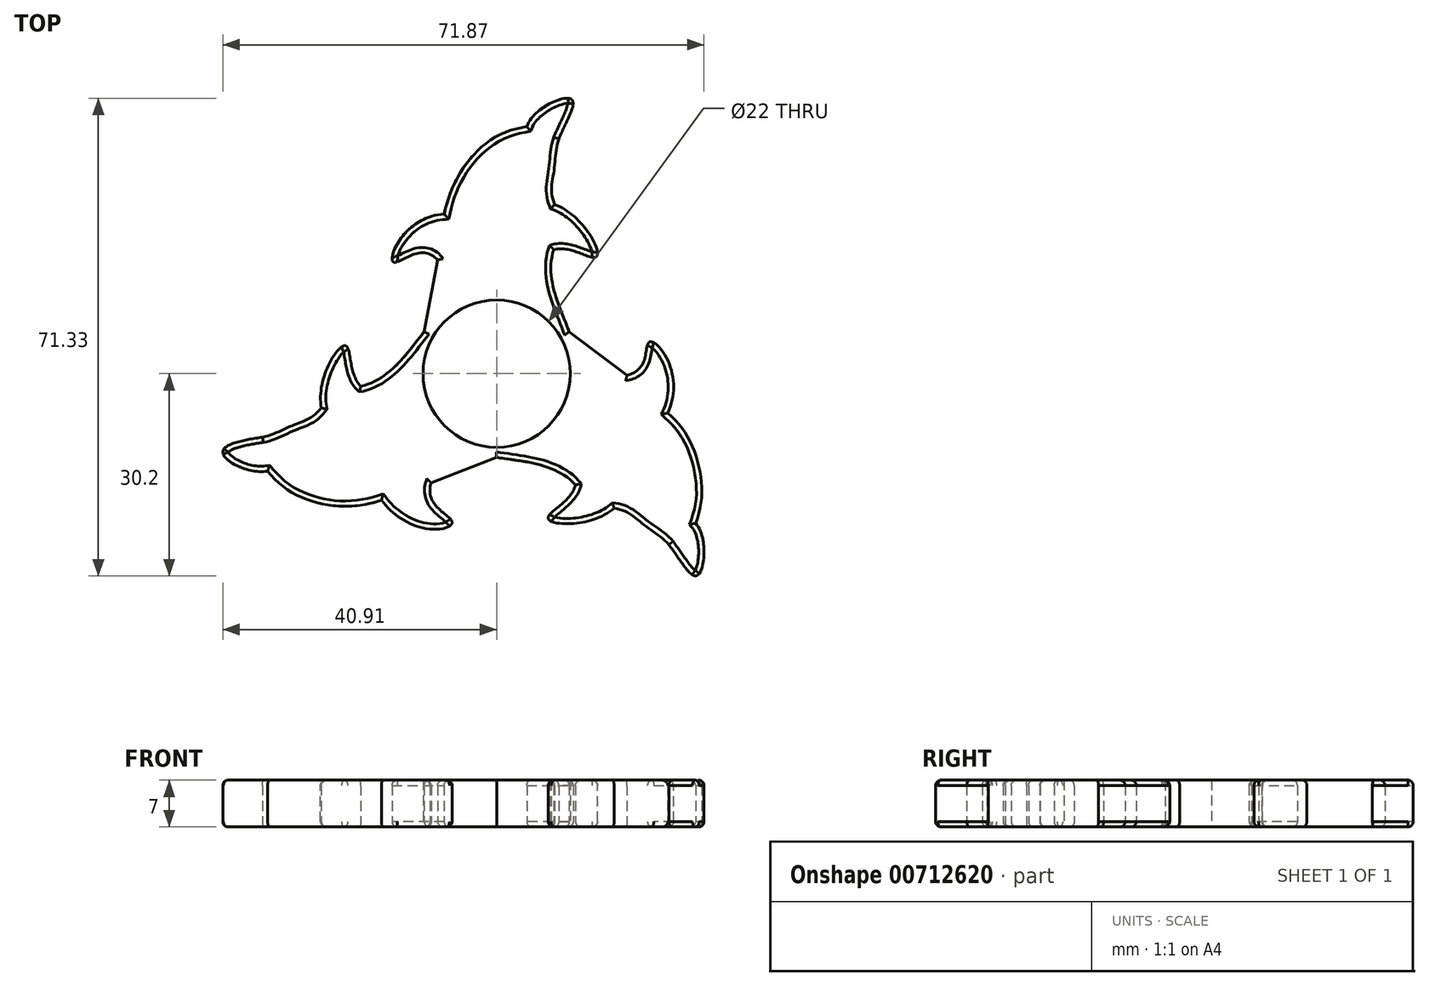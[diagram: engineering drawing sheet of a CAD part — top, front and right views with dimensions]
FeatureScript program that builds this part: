
annotation { "Feature Type Name" : "Feature", "Feature Type Description" : "" }
export const myFeature = defineFeature(function(context is Context, id is Id, definition is map)
    precondition{}
    {
        {
            var Q0;
            Q0=qCreatedBy(makeId("Top.planeOp"),FACE);
            var sketch = newSketch(context, id + "F0", { "sketchPlane" : qUnion([Q0])});
            skLineSegment(sketch, "E0", {"start": v(-52.16, -31.34) * mm, "end": v(59.27, 35.61) * mm, "construction": true});
            skLineSegment(sketch, "E1", {"start": v(-57.19, 34.36) * mm, "end": v(54.24, -32.6) * mm, "construction": true});
            skCircle(sketch, "E2", {"center": v(0, 0) * mm, "radius": 11 * mm});
            skCircle(sketch, "E3", {"center": v(0, 0) * mm, "radius": 12.5 * mm});
            skFitSpline(sketch, "E4.MirrorCS", {"points": [v(-20.28, -1.87) * mm, v(-15.58, 0.7) * mm, v(-10.83, 6.25) * mm], "startDerivative": vector(9.48, 1.73) * mm, "endDerivative": vector(6.62, 8.07) * mm});
            skFitSpline(sketch, "E5.MirrorCS", {"points": [v(-26.18, -5.12) * mm, v(-22.57, 4.17) * mm, v(-20.28, -1.87) * mm], "startDerivative": vector(-4.53, 23.16) * mm, "endDerivative": vector(12.61, -12.05) * mm});
            skFitSpline(sketch, "E6.MirrorCS", {"points": [v(-34.97, -9.49) * mm, v(-30.3, -7.66) * mm, v(-26.18, -5.12) * mm], "startDerivative": vector(8.1, 1.22) * mm, "endDerivative": vector(8.17, 10.27) * mm});
            skFitSpline(sketch, "E7.MirrorCS", {"points": [v(-34.97, -9.49) * mm, v(-40.9, -11.76) * mm, v(-34.2, -14.55) * mm], "startDerivative": vector(-17.23, -2.37) * mm, "endDerivative": vector(15.94, 3.1) * mm});
            skFitSpline(sketch, "E8.MirrorCS", {"points": [v(-34.2, -14.55) * mm, v(-27.19, -19.17) * mm, v(-17.22, -18.9) * mm], "startDerivative": vector(13.23, -16.41) * mm, "endDerivative": vector(22.4, 7.3) * mm});
            skFitSpline(sketch, "E9.MirrorCS", {"points": [v(-17.22, -18.9) * mm, v(-6.67, -22.17) * mm, v(-9.79, -16.3) * mm], "startDerivative": vector(23, -30) * mm, "endDerivative": vector(7.72, 24) * mm});
            skLineSegment(sketch, "E10.MirrorCS", {"start": v(-9.79, -16.3) * mm, "end": v(0, -12.5) * mm});
            skFitSpline(sketch, "E11.MirrorCS", {"points": [v(29.7, -22.35) * mm, v(30.2, -13.96) * mm, v(25.56, -5.88) * mm], "startDerivative": vector(7.6, 19.67) * mm, "endDerivative": vector(-17.53, 15.74) * mm});
            skFitSpline(sketch, "E12.MirrorCS", {"points": [v(25.56, -5.88) * mm, v(22.8, 4.7) * mm, v(19.46, -0.22) * mm], "startDerivative": vector(13.83, 30.64) * mm, "endDerivative": vector(-24.36, -4.82) * mm});
            skFitSpline(sketch, "E13.MirrorCS", {"points": [v(25.7, -25.54) * mm, v(29.94, -30.14) * mm, v(29.7, -22.35) * mm], "startDerivative": vector(10.67, -13.74) * mm, "endDerivative": vector(-10.65, 12.26) * mm});
            skFitSpline(sketch, "E14.MirrorCS", {"points": [v(25.7, -25.54) * mm, v(21.79, -22.42) * mm, v(17.53, -20.11) * mm], "startDerivative": vector(-5.11, 6.41) * mm, "endDerivative": vector(-12.98, 1.94) * mm});
            skFitSpline(sketch, "E15.MirrorCS", {"points": [v(17.53, -20.11) * mm, v(7.68, -21.63) * mm, v(11.76, -16.63) * mm], "startDerivative": vector(-17.8, -15.5) * mm, "endDerivative": vector(4.13, 16.95) * mm});
            skFitSpline(sketch, "E16.MirrorCS", {"points": [v(11.76, -16.63) * mm, v(7.2, -13.84) * mm, v(0, -12.5) * mm], "startDerivative": vector(-6.23, 7.34) * mm, "endDerivative": vector(-10.3, 1.7) * mm});
            skLineSegment(sketch, "E17.MirrorCS", {"start": v(19.46, -0.22) * mm, "end": v(10.83, 6.25) * mm});
            skLineSegment(sketch, "E18", {"start": v(-28.35, 41) * mm, "end": v(37.86, 41) * mm, "construction": true});
            skFitSpline(sketch, "E19.MirrorCS", {"points": [v(8.52, 18.5) * mm, v(8.39, 13.15) * mm, v(10.83, 6.25) * mm], "startDerivative": vector(-3.24, -9.07) * mm, "endDerivative": vector(3.68, -9.77) * mm});
            skFitSpline(sketch, "E20.MirrorCS", {"points": [v(8.65, 25.24) * mm, v(14.9, 17.46) * mm, v(8.52, 18.5) * mm], "startDerivative": vector(22.32, -7.65) * mm, "endDerivative": vector(-16.74, -4.9) * mm});
            skFitSpline(sketch, "E21.MirrorCS", {"points": [v(9.27, 35.03) * mm, v(8.52, 30.08) * mm, v(8.65, 25.24) * mm], "startDerivative": vector(-3, -7.63) * mm, "endDerivative": vector(4.8, -12.2) * mm});
            skFitSpline(sketch, "E22.MirrorCS", {"points": [v(9.27, 35.03) * mm, v(11.13, 41) * mm, v(4.5, 36.9) * mm], "startDerivative": vector(6.56, 16.1) * mm, "endDerivative": vector(-5.3, -15.35) * mm});
            skFitSpline(sketch, "E23.MirrorCS", {"points": [v(4.5, 36.9) * mm, v(-3, 33.13) * mm, v(-7.84, 23.82) * mm], "startDerivative": vector(-20.83, -3.25) * mm, "endDerivative": vector(-4.87, -23.05) * mm});
            skFitSpline(sketch, "E24.MirrorCS", {"points": [v(-7.84, 23.82) * mm, v(-15.38, 16.64) * mm, v(-8.82, 16.96) * mm], "startDerivative": vector(-32.1, -1.97) * mm, "endDerivative": vector(16.35, -18.69) * mm});
            skLineSegment(sketch, "E25.MirrorCS", {"start": v(-8.82, 16.96) * mm, "end": v(-10.83, 6.25) * mm});
            skSolve(sketch);
        }
        {
            var Q0;
            Q0 = qSketchRegion(id + "F0", true);
            extrude(context, id + "F1", {"entities" : qUnion([Q0]), "depth" : 7 * mm, "offsetDistance" : 25 * mm});
        }
        {
            var Q0;
            Q0=makeQuery(id+"F1.opExtrude","CAP_EDGE",EDGE,{"disambiguationData":[OSD([sQuery(id+"F0.wireOp",EDGE,"E23.MirrorCS")])],"isStart":false});
            var Q1;
            Q1=makeQuery(id+"F1.opExtrude","CAP_EDGE",EDGE,{"disambiguationData":[OSD([sQuery(id+"F0.wireOp",EDGE,"E21.MirrorCS")])],"isStart":false});
            var Q2;
            Q2=makeQuery(id+"F1.opExtrude","CAP_EDGE",EDGE,{"disambiguationData":[OSD([sQuery(id+"F0.wireOp",EDGE,"E19.MirrorCS")])],"isStart":false});
            var Q3;
            Q3=makeQuery(id+"F1.opExtrude","CAP_EDGE",EDGE,{"disambiguationData":[OSD([sQuery(id+"F0.wireOp",EDGE,"E25.MirrorCS")])],"isStart":false});
            var Q4;
            Q4=makeQuery(id+"F1.opExtrude","CAP_EDGE",EDGE,{"disambiguationData":[OSD([sQuery(id+"F0.wireOp",EDGE,"E4.MirrorCS")])],"isStart":false});
            var Q5;
            Q5=makeQuery(id+"F1.opExtrude","CAP_EDGE",EDGE,{"disambiguationData":[OSD([sQuery(id+"F0.wireOp",EDGE,"0862ff20-f81b-441f-8cea-de6020e5842e0.MirrorCS")])],"isStart":false});
            var Q6;
            Q6=makeQuery(id+"F1.opExtrude","CAP_EDGE",EDGE,{"disambiguationData":[OSD([sQuery(id+"F0.wireOp",EDGE,"E17.MirrorCS")])],"isStart":false});
            var Q7;
            Q7=makeQuery(id+"F1.opExtrude","CAP_EDGE",EDGE,{"disambiguationData":[OSD([sQuery(id+"F0.wireOp",EDGE,"E11.MirrorCS")])],"isStart":false});
            var Q8;
            Q8=makeQuery(id+"F1.opExtrude","CAP_EDGE",EDGE,{"disambiguationData":[OSD([sQuery(id+"F0.wireOp",EDGE,"E14.MirrorCS")])],"isStart":false});
            var Q9;
            Q9=makeQuery(id+"F1.opExtrude","CAP_EDGE",EDGE,{"disambiguationData":[OSD([sQuery(id+"F0.wireOp",EDGE,"E16.MirrorCS")])],"isStart":false});
            var Q10;
            Q10=makeQuery(id+"F1.opExtrude","CAP_EDGE",EDGE,{"disambiguationData":[OSD([sQuery(id+"F0.wireOp",EDGE,"E10.MirrorCS")])],"isStart":false});
            var Q11;
            Q11=makeQuery(id+"F1.opExtrude","CAP_EDGE",EDGE,{"disambiguationData":[OSD([sQuery(id+"F0.wireOp",EDGE,"E8.MirrorCS")])],"isStart":false});
            var Q12;
            Q12=makeQuery(id+"F1.opExtrude","CAP_EDGE",EDGE,{"disambiguationData":[OSD([sQuery(id+"F0.wireOp",EDGE,"E6.MirrorCS")])],"isStart":false});
            var Q13;
            Q13=makeQuery(id+"F1.opExtrude","CAP_EDGE",EDGE,{"disambiguationData":[OSD([sQuery(id+"F0.wireOp",EDGE,"E15.MirrorCS")])],"isStart":false});
            var Q14;
            Q14=makeQuery(id+"F1.opExtrude","CAP_EDGE",EDGE,{"disambiguationData":[OSD([sQuery(id+"F0.wireOp",EDGE,"E5.MirrorCS")])],"isStart":false});
            var Q15;
            Q15=makeQuery(id+"F1.opExtrude","CAP_EDGE",EDGE,{"disambiguationData":[OSD([sQuery(id+"F0.wireOp",EDGE,"E20.MirrorCS")])],"isStart":false});
            var Q16;
            Q16=makeQuery(id+"F1.opExtrude","CAP_EDGE",EDGE,{"disambiguationData":[OSD([sQuery(id+"F0.wireOp",EDGE,"E13.MirrorCS")])],"isStart":false});
            var Q17;
            Q17=makeQuery(id+"F1.opExtrude","CAP_EDGE",EDGE,{"disambiguationData":[OSD([sQuery(id+"F0.wireOp",EDGE,"E7.MirrorCS")])],"isStart":false});
            var Q18;
            Q18=makeQuery(id+"F1.opExtrude","CAP_EDGE",EDGE,{"disambiguationData":[OSD([sQuery(id+"F0.wireOp",EDGE,"E22.MirrorCS")])],"isStart":false});
            var Q19;
            Q19=makeQuery(id+"F1.opExtrude","CAP_EDGE",EDGE,{"disambiguationData":[OSD([sQuery(id+"F0.wireOp",EDGE,"E22.MirrorCS")])],"isStart":true});
            var Q20;
            Q20=makeQuery(id+"F1.opExtrude","CAP_EDGE",EDGE,{"disambiguationData":[OSD([sQuery(id+"F0.wireOp",EDGE,"E23.MirrorCS")])],"isStart":true});
            var Q21;
            Q21=makeQuery(id+"F1.opExtrude","CAP_EDGE",EDGE,{"disambiguationData":[OSD([sQuery(id+"F0.wireOp",EDGE,"E21.MirrorCS")])],"isStart":true});
            var Q22;
            Q22=makeQuery(id+"F1.opExtrude","CAP_EDGE",EDGE,{"disambiguationData":[OSD([sQuery(id+"F0.wireOp",EDGE,"E19.MirrorCS")])],"isStart":true});
            var Q23;
            Q23=makeQuery(id+"F1.opExtrude","CAP_EDGE",EDGE,{"disambiguationData":[OSD([sQuery(id+"F0.wireOp",EDGE,"E17.MirrorCS")])],"isStart":true});
            var Q24;
            Q24=makeQuery(id+"F1.opExtrude","CAP_EDGE",EDGE,{"disambiguationData":[OSD([sQuery(id+"F0.wireOp",EDGE,"E25.MirrorCS")])],"isStart":true});
            var Q25;
            Q25=makeQuery(id+"F1.opExtrude","CAP_EDGE",EDGE,{"disambiguationData":[OSD([sQuery(id+"F0.wireOp",EDGE,"0862ff20-f81b-441f-8cea-de6020e5842e0.MirrorCS")])],"isStart":true});
            var Q26;
            Q26=makeQuery(id+"F1.opExtrude","CAP_EDGE",EDGE,{"disambiguationData":[OSD([sQuery(id+"F0.wireOp",EDGE,"E4.MirrorCS")])],"isStart":true});
            var Q27;
            Q27=makeQuery(id+"F1.opExtrude","CAP_EDGE",EDGE,{"disambiguationData":[OSD([sQuery(id+"F0.wireOp",EDGE,"E6.MirrorCS")])],"isStart":true});
            var Q28;
            Q28=makeQuery(id+"F1.opExtrude","CAP_EDGE",EDGE,{"disambiguationData":[OSD([sQuery(id+"F0.wireOp",EDGE,"E8.MirrorCS")])],"isStart":true});
            var Q29;
            Q29=makeQuery(id+"F1.opExtrude","CAP_EDGE",EDGE,{"disambiguationData":[OSD([sQuery(id+"F0.wireOp",EDGE,"E10.MirrorCS")])],"isStart":true});
            var Q30;
            Q30=makeQuery(id+"F1.opExtrude","CAP_EDGE",EDGE,{"disambiguationData":[OSD([sQuery(id+"F0.wireOp",EDGE,"E16.MirrorCS")])],"isStart":true});
            var Q31;
            Q31=makeQuery(id+"F1.opExtrude","CAP_EDGE",EDGE,{"disambiguationData":[OSD([sQuery(id+"F0.wireOp",EDGE,"E15.MirrorCS")])],"isStart":true});
            var Q32;
            Q32=makeQuery(id+"F1.opExtrude","CAP_EDGE",EDGE,{"disambiguationData":[OSD([sQuery(id+"F0.wireOp",EDGE,"E14.MirrorCS")])],"isStart":true});
            var Q33;
            Q33=makeQuery(id+"F1.opExtrude","CAP_EDGE",EDGE,{"disambiguationData":[OSD([sQuery(id+"F0.wireOp",EDGE,"E13.MirrorCS")])],"isStart":true});
            var Q34;
            Q34=makeQuery(id+"F1.opExtrude","CAP_EDGE",EDGE,{"disambiguationData":[OSD([sQuery(id+"F0.wireOp",EDGE,"E11.MirrorCS")])],"isStart":true});
            var Q35;
            Q35=makeQuery(id+"F1.opExtrude","CAP_EDGE",EDGE,{"disambiguationData":[OSD([sQuery(id+"F0.wireOp",EDGE,"E20.MirrorCS")])],"isStart":true});
            var Q36;
            Q36=makeQuery(id+"F1.opExtrude","CAP_EDGE",EDGE,{"disambiguationData":[OSD([sQuery(id+"F0.wireOp",EDGE,"E5.MirrorCS")])],"isStart":true});
            var Q37;
            Q37=makeQuery(id+"F1.opExtrude","CAP_EDGE",EDGE,{"disambiguationData":[OSD([sQuery(id+"F0.wireOp",EDGE,"E7.MirrorCS")])],"isStart":true});
            var Q38;
            Q38=makeQuery(id+"F1.opExtrude","CAP_EDGE",EDGE,{"disambiguationData":[OSD([sQuery(id+"F0.wireOp",EDGE,"E24.MirrorCS")])],"isStart":false});
            var Q39;
            Q39=makeQuery(id+"F1.opExtrude","CAP_EDGE",EDGE,{"disambiguationData":[OSD([sQuery(id+"F0.wireOp",EDGE,"E24.MirrorCS")])],"isStart":true});
            var Q40;
            Q40=makeQuery(id+"F1.opExtrude","CAP_EDGE",EDGE,{"disambiguationData":[OSD([sQuery(id+"F0.wireOp",EDGE,"E12.MirrorCS")])],"isStart":true});
            var Q41;
            Q41=makeQuery(id+"F1.opExtrude","CAP_EDGE",EDGE,{"disambiguationData":[OSD([sQuery(id+"F0.wireOp",EDGE,"E12.MirrorCS")])],"isStart":false});
            var Q42;
            Q42=makeQuery(id+"F1.opExtrude","CAP_EDGE",EDGE,{"disambiguationData":[OSD([sQuery(id+"F0.wireOp",EDGE,"E9.MirrorCS")])],"isStart":false});
            var Q43;
            Q43=makeQuery(id+"F1.opExtrude","CAP_EDGE",EDGE,{"disambiguationData":[OSD([sQuery(id+"F0.wireOp",EDGE,"E9.MirrorCS")])],"isStart":true});
            fillet(context, id + "F2", {"entities" : qUnion([Q0, Q1, Q2, Q3, Q4, Q5, Q6, Q7, Q8, Q9, Q10, Q11, Q12, Q13, Q14, Q15, Q16, Q17, Q18, Q19, Q20, Q21, Q22, Q23, Q24, Q25, Q26, Q27, Q28, Q29, Q30, Q31, Q32, Q33, Q34, Q35, Q36, Q37, Q38, Q39, Q40, Q41, Q42, Q43]), "radius" : .8 * mm, "tangentPropagation" : true, "allowEdgeOverflow" : false});
        }
    });
